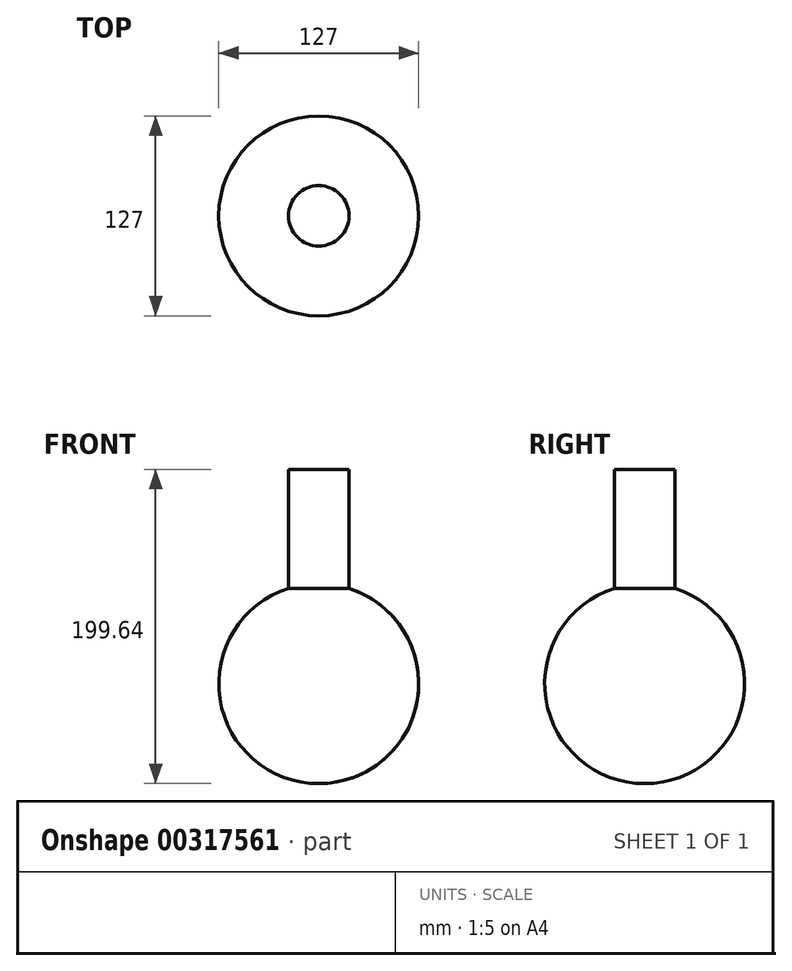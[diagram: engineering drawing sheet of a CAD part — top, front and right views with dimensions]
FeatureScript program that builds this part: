
annotation { "Feature Type Name" : "Feature", "Feature Type Description" : "" }
export const myFeature = defineFeature(function(context is Context, id is Id, definition is map)
    precondition{}
    {
        {
            var Q0;
            Q0=qCreatedBy(makeId("Front.planeOp"),FACE);
            var sketch = newSketch(context, id + "F0", { "sketchPlane" : qUnion([Q0])});
            skArc(sketch, "E0", {"start": v(0, 63.5) * mm, "mid": v(-63.5, 0) * mm, "end": v(0, -63.5) * mm});
            skLineSegment(sketch, "E1", {"start": v(0, 0) * mm, "end": v(0, 63.5) * mm});
            skLineSegment(sketch, "E2", {"start": v(0, 63.5) * mm, "end": v(0, 0) * mm});
            skLineSegment(sketch, "E3", {"start": v(0, 0) * mm, "end": v(0, -63.5) * mm});
            skSolve(sketch);
        }
        {
            var Q0;
            Q0=qCreatedBy(makeId("Front.planeOp"),FACE);
            var sketch = newSketch(context, id + "F1", { "sketchPlane" : qUnion([Q0])});
            skLineSegment(sketch, "E4", {"start": v(0, 0) * mm, "end": v(0, -63.25) * mm});
            skLineSegment(sketch, "E5", {"start": v(0, 0) * mm, "end": v(0, 62.03) * mm});
            skLineSegment(sketch, "E6", {"start": v(0, 62.03) * mm, "end": v(0, 0) * mm});
            skSolve(sketch);
        }
        {
            var Q0;
            Q0 = qSketchRegion(id + "F0", true);
            var Q1;
            Q1=sQuery(id+"F1.wireOp",EDGE,"E6");
            revolve(context, id + "F2", {"entities" : qUnion([Q0]), "axis" : qUnion([Q1]), "revolveType" : RevolveType.FULL});
        }
        {
            var Q0;
            Q0=qCreatedBy(makeId("Top.planeOp"),FACE);
            var sketch = newSketch(context, id + "F3", { "sketchPlane" : qUnion([Q0])});
            skCircle(sketch, "E7", {"center": v(0, 0) * mm, "radius": 19.2 * mm});
            skSolve(sketch);
        }
        {
            var Q0;
            Q0 = qSketchRegion(id + "F3", true);
            extrude(context, id + "F4", {"entities" : qUnion([Q0]), "operationType" : NewBodyOperationType.ADD, "depth" : 136.14 * mm});
        }
    });
